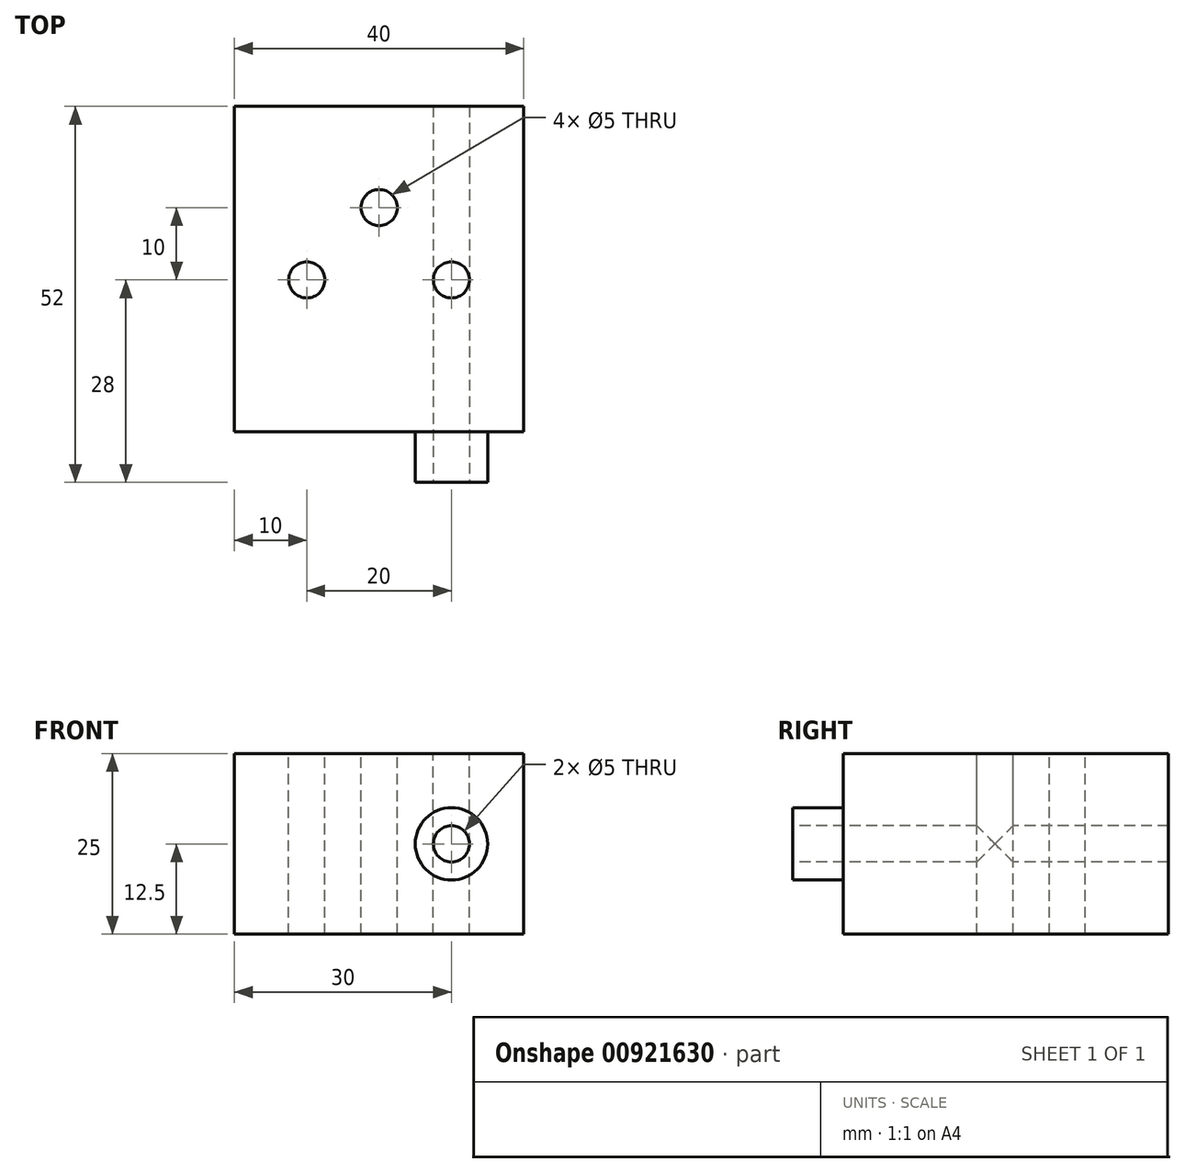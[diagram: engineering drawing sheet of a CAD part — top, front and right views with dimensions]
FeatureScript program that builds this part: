
annotation { "Feature Type Name" : "Feature", "Feature Type Description" : "" }
export const myFeature = defineFeature(function(context is Context, id is Id, definition is map)
    precondition{}
    {
        {
            var Q0;
            Q0=qCreatedBy(makeId("Front.planeOp"),FACE);
            var sketch = newSketch(context, id + "F0", { "sketchPlane" : qUnion([Q0])});
            skLineSegment(sketch, "E0.bottom", {"start": v(-30, 12.5) * mm, "end": v(10, 12.5) * mm});
            skLineSegment(sketch, "E0.top", {"start": v(-30, -12.5) * mm, "end": v(10, -12.5) * mm});
            skLineSegment(sketch, "E0.left", {"start": v(-30, 12.5) * mm, "end": v(-30, -12.5) * mm});
            skLineSegment(sketch, "E0.right", {"start": v(10, 12.5) * mm, "end": v(10, -12.5) * mm});
            skPoint(sketch, "E1", {"position": v(-10, -12.5) * mm});
            skLineSegment(sketch, "E2", {"start": v(0, 0) * mm, "end": v(18.5, 0) * mm, "construction": true});
            skCircle(sketch, "E3", {"center": v(0, 0) * mm, "radius": 2.5 * mm, "construction": true});
            skSolve(sketch);
        }
        {
            var Q0;
            Q0 = qSketchRegion(id + "F0", true);
            extrude(context, id + "F1", {"entities" : qUnion([Q0]), "oppositeDirection" : true, "depth" : 45 * mm, "offsetDistance" : 25 * mm});
        }
        {
            var Q0;
            Q0=makeQuery(id+"F0.imprint","IMPRINT",FACE,{"disambiguationData":[TD([[makeQuery(id+"F0.imprint","IMPRINT",EDGE,{"derivedFrom":sQuery(id+"F0.wireOp",EDGE,"E0.bottom")}),-1.0]])]});
            var sketch = newSketch(context, id + "F2", { "sketchPlane" : qUnion([Q0])});
            skCircle(sketch, "E4", {"center": v(0, 0) * mm, "radius": 5 * mm});
            skSolve(sketch);
        }
        {
            var Q0;
            Q0 = qSketchRegion(id + "F2", true);
            extrude(context, id + "F3", {"entities" : qUnion([Q0]), "operationType" : NewBodyOperationType.ADD, "depth" : 7 * mm, "offsetDistance" : 25 * mm});
        }
        {
            var Q0;
            Q0=qCreatedBy(makeId("Front.planeOp"),FACE);
            var sketch = newSketch(context, id + "F4", { "sketchPlane" : qUnion([Q0])});
            skCircle(sketch, "E5.0", {"center": v(0, 0) * mm, "radius": 2.5 * mm});
            skSolve(sketch);
        }
        {
            var Q0;
            Q0 = qSketchRegion(id + "F4", true);
            extrude(context, id + "F5", {"entities" : qUnion([Q0]), "operationType" : NewBodyOperationType.REMOVE, "endBound" : BoundingType.THROUGH_ALL, "oppositeDirection" : true, "depth" : 25 * mm, "offsetDistance" : 25 * mm, "hasSecondDirection" : true, "secondDirectionBound" : SecondDirectionBoundingType.THROUGH_ALL, "secondDirectionOppositeDirection" : false, "secondDirectionDepth" : 25 * mm});
        }
        {
            var Q0;
            Q0=makeQuery(id+"F1.opExtrude","SWEPT_FACE",FACE,{"disambiguationData":[OSD([sQuery(id+"F0.wireOp",EDGE,"E0.bottom")])]});
            var sketch = newSketch(context, id + "F6", { "sketchPlane" : qUnion([Q0])});
            skCircle(sketch, "E6", {"center": v(0, 21) * mm, "radius": 2.5 * mm});
            skCircle(sketch, "E7", {"center": v(-10, 31) * mm, "radius": 2.5 * mm});
            skCircle(sketch, "E8", {"center": v(-20, 21) * mm, "radius": 2.5 * mm});
            skSolve(sketch);
        }
        {
            var Q0;
            Q0 = qSketchRegion(id + "F6", true);
            extrude(context, id + "F7", {"entities" : qUnion([Q0]), "operationType" : NewBodyOperationType.REMOVE, "endBound" : BoundingType.THROUGH_ALL, "oppositeDirection" : true, "depth" : 5 * mm, "offsetDistance" : 25 * mm});
        }
    });
